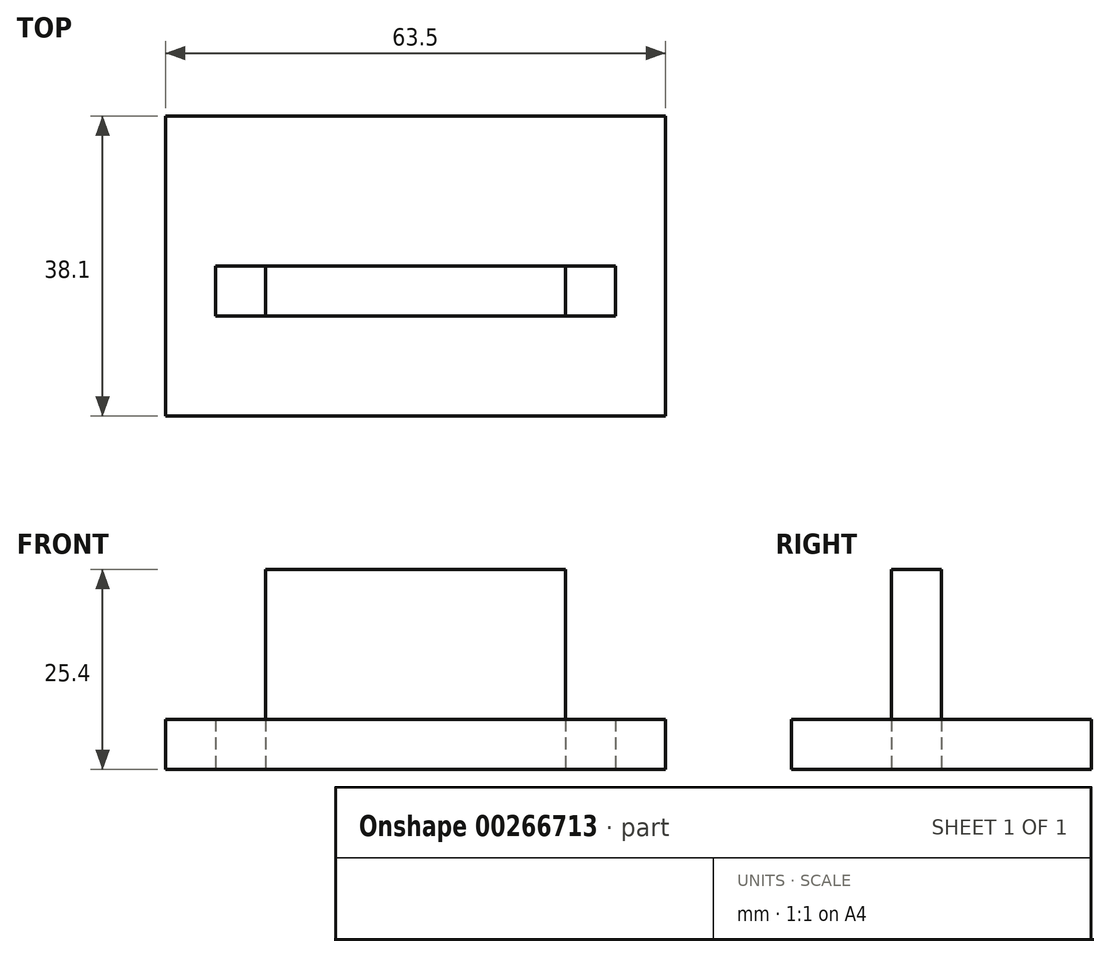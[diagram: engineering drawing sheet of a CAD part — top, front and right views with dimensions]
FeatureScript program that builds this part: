
annotation { "Feature Type Name" : "Feature", "Feature Type Description" : "" }
export const myFeature = defineFeature(function(context is Context, id is Id, definition is map)
    precondition{}
    {
        {
            var Q0;
            Q0=qCreatedBy(makeId("Top.planeOp"),FACE);
            var sketch = newSketch(context, id + "F0", { "sketchPlane" : qUnion([Q0])});
            skLineSegment(sketch, "E0.bottom", {"start": v(-31.75, 19.05) * mm, "end": v(31.75, 19.05) * mm});
            skLineSegment(sketch, "E0.top", {"start": v(-31.75, -19.05) * mm, "end": v(31.75, -19.05) * mm});
            skLineSegment(sketch, "E0.left", {"start": v(-31.75, 19.05) * mm, "end": v(-31.75, -19.05) * mm});
            skLineSegment(sketch, "E0.right", {"start": v(31.75, 19.05) * mm, "end": v(31.75, -19.05) * mm});
            skPoint(sketch, "E0.middle", {"position": v(0, 0) * mm});
            skLineSegment(sketch, "E1.bottom", {"start": v(-25.4, 0) * mm, "end": v(-19.05, 0) * mm});
            skLineSegment(sketch, "E1.top", {"start": v(-25.4, -19.05) * mm, "end": v(-19.05, -19.05) * mm});
            skLineSegment(sketch, "E1.left", {"start": v(-25.4, 0) * mm, "end": v(-25.4, -19.05) * mm});
            skLineSegment(sketch, "E1.right", {"start": v(-19.05, 0) * mm, "end": v(-19.05, -19.05) * mm});
            skLineSegment(sketch, "E2.top", {"start": v(19.05, -19.05) * mm, "end": v(25.4, -19.05) * mm});
            skLineSegment(sketch, "E3.bottom", {"start": v(-25.4, 0) * mm, "end": v(25.4, 0) * mm});
            skLineSegment(sketch, "E3.top", {"start": v(-25.4, -6.35) * mm, "end": v(25.4, -6.35) * mm});
            skLineSegment(sketch, "E3.left", {"start": v(-25.4, 0) * mm, "end": v(-25.4, -6.35) * mm});
            skLineSegment(sketch, "E3.right", {"start": v(25.4, 0) * mm, "end": v(25.4, -6.35) * mm});
            skLineSegment(sketch, "E4.bottom", {"start": v(25.4, 0) * mm, "end": v(19.05, 0) * mm});
            skLineSegment(sketch, "E4.top", {"start": v(25.4, -19.05) * mm, "end": v(19.05, -19.05) * mm});
            skLineSegment(sketch, "E4.left", {"start": v(25.4, 0) * mm, "end": v(25.4, -19.05) * mm});
            skLineSegment(sketch, "E4.right", {"start": v(19.05, 0) * mm, "end": v(19.05, -19.05) * mm});
            skSolve(sketch);
        }
        {
            var Q0;
            {var subQ5=sQuery(id+"F0.wireOp",EDGE,"E4.top");Q0=makeQuery(id+"F0.imprint","IMPRINT",FACE,{"disambiguationData":[TD([[makeQuery(id+"F0.imprint","IMPRINT",EDGE,{"derivedFrom":subQ5}),-1.0]])]});}
            var Q1;
            {var subQ5=sQuery(id+"F0.wireOp",EDGE,"E4.bottom");Q1=makeQuery(id+"F0.imprint","IMPRINT",FACE,{"disambiguationData":[TD([[makeQuery(id+"F0.imprint","IMPRINT",EDGE,{"derivedFrom":subQ5}),1.0]])]});}
            var Q2;
            {var subQ0=sQuery(id+"F0.wireOp",EDGE,"E3.bottom");var subQ1=sQuery(id+"F0.wireOp",EDGE,"E1.right");var subQ2=makeQuery(id+"F0.imprint","INTERSECT",VERTEX,{"derivedFrom":[subQ1,subQ0]});Q2=makeQuery(id+"F0.imprint","IMPRINT",FACE,{"disambiguationData":[TD([[makeQuery(id+"F0.imprint","IMPRINT",EDGE,{"disambiguationData":[TD([[subQ2,-1.0]])],"derivedFrom":subQ1}),1.0]])]});}
            var Q3;
            {var subQ5=sQuery(id+"F0.wireOp",EDGE,"E3.left");Q3=makeQuery(id+"F0.imprint","IMPRINT",FACE,{"disambiguationData":[TD([[makeQuery(id+"F0.imprint","IMPRINT",EDGE,{"derivedFrom":subQ5}),1.0]])]});}
            var Q4;
            {var subQ0=sQuery(id+"F0.wireOp",EDGE,"E1.top");Q4=makeQuery(id+"F0.imprint","IMPRINT",FACE,{"disambiguationData":[TD([[makeQuery(id+"F0.imprint","IMPRINT",EDGE,{"derivedFrom":subQ0}),1.0]])]});}
            extrude(context, id + "F1", {"entities" : qUnion([Q0, Q1, Q2, Q3, Q4]), "depth" : 25.4 * mm});
        }
        {
            var Q0;
            Q0 = qSketchRegion(id + "F0", true);
            extrude(context, id + "F2", {"entities" : qUnion([Q0]), "operationType" : NewBodyOperationType.ADD, "depth" : 6.35 * mm});
        }
    });
